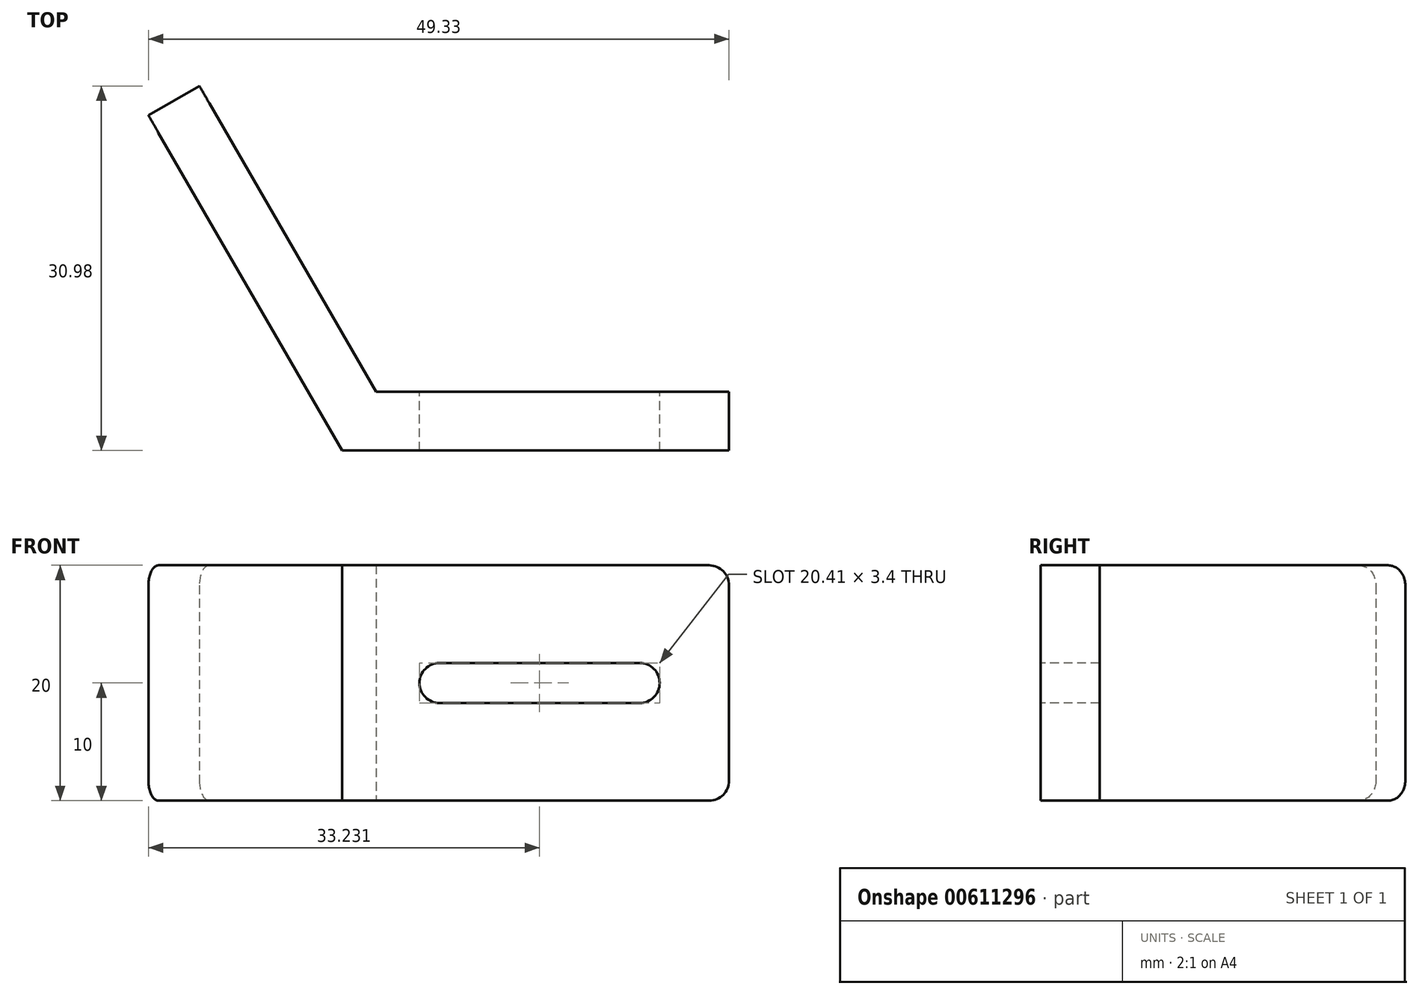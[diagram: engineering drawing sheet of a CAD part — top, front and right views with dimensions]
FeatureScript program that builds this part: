
annotation { "Feature Type Name" : "Feature", "Feature Type Description" : "" }
export const myFeature = defineFeature(function(context is Context, id is Id, definition is map)
    precondition{}
    {
        {
            var Q0;
            Q0=qCreatedBy(makeId("Top.planeOp"),FACE);
            var sketch = newSketch(context, id + "F0", { "sketchPlane" : qUnion([Q0])});
            skLineSegment(sketch, "E0", {"start": v(0, 0) * mm, "end": v(30, 0) * mm});
            skLineSegment(sketch, "E1", {"start": v(30, 0) * mm, "end": v(30, 5) * mm});
            skLineSegment(sketch, "E2", {"start": v(30, 5) * mm, "end": v(0, 5) * mm});
            skLineSegment(sketch, "E3", {"start": v(0, 5) * mm, "end": v(-15, 30.98) * mm});
            skLineSegment(sketch, "E4", {"start": v(-15, 30.98) * mm, "end": v(-19.33, 28.48) * mm});
            skLineSegment(sketch, "E5", {"start": v(0, 0) * mm, "end": v(-2.89, 0) * mm});
            skLineSegment(sketch, "E6", {"start": v(-2.89, 0) * mm, "end": v(-19.33, 28.48) * mm});
            skSolve(sketch);
        }
        {
            var Q0;
            Q0=makeQuery(id+"F0.imprint","IMPRINT",FACE,{"disambiguationData":[TD([[makeQuery(id+"F0.imprint","IMPRINT",EDGE,{"derivedFrom":sQuery(id+"F0.wireOp",EDGE,"E0")}),1.0]])]});
            extrude(context, id + "F1", {"entities" : qUnion([Q0]), "depth" : 20 * mm, "offsetDistance" : 25 * mm});
        }
        {
            var Q0;
            Q0=makeQuery(id+"F1.opExtrude","SWEPT_FACE",FACE,{"disambiguationData":[OSD([sQuery(id+"F0.wireOp",EDGE,"E0"),sQuery(id+"F0.wireOp",EDGE,"E5")])]});
            var sketch = newSketch(context, id + "F2", { "sketchPlane" : qUnion([Q0])});
            skLineSegment(sketch, "E7.bottom", {"start": v(24.1, 8.3) * mm, "end": v(3.7, 8.3) * mm});
            skLineSegment(sketch, "E7.top", {"start": v(24.1, 11.7) * mm, "end": v(3.7, 11.7) * mm});
            skLineSegment(sketch, "E7.left", {"start": v(24.1, 8.3) * mm, "end": v(24.1, 11.7) * mm});
            skLineSegment(sketch, "E7.right", {"start": v(3.7, 8.3) * mm, "end": v(3.7, 11.7) * mm});
            skPoint(sketch, "E7.middle", {"position": v(13.9, 10) * mm});
            skPoint(sketch, "E7.middle.positionSnap0", {"position": v(30, 10) * mm});
            skPoint(sketch, "E7.centerSnap0", {"position": v(30, 10) * mm});
            skSolve(sketch);
        }
        {
            var Q0;
            Q0=makeQuery(id+"F2.imprint","IMPRINT",FACE,{"disambiguationData":[TD([[makeQuery(id+"F2.imprint","IMPRINT",EDGE,{"derivedFrom":sQuery(id+"F2.wireOp",EDGE,"E7.bottom")}),-1.0]])]});
            extrude(context, id + "F3", {"entities" : qUnion([Q0]), "operationType" : NewBodyOperationType.REMOVE, "oppositeDirection" : true, "depth" : 25 * mm, "offsetDistance" : 25 * mm});
        }
        {
            var Q0;
            Q0=makeQuery(id+"F3.boolean.opBoolean","COPY",EDGE,{"derivedFrom":makeQuery(id+"F3.opExtrude","SWEPT_EDGE",EDGE,{"disambiguationData":[OSD([sQuery(id+"F2.wireOp",EDGE,"E7.bottom"),sQuery(id+"F2.wireOp",EDGE,"E7.right")])]})});
            var Q1;
            Q1=makeQuery(id+"F3.boolean.opBoolean","COPY",EDGE,{"derivedFrom":makeQuery(id+"F3.opExtrude","SWEPT_EDGE",EDGE,{"disambiguationData":[OSD([sQuery(id+"F2.wireOp",EDGE,"E7.top"),sQuery(id+"F2.wireOp",EDGE,"E7.right")])]})});
            var Q2;
            Q2=makeQuery(id+"F3.boolean.opBoolean","COPY",EDGE,{"derivedFrom":makeQuery(id+"F3.opExtrude","SWEPT_EDGE",EDGE,{"disambiguationData":[OSD([sQuery(id+"F2.wireOp",EDGE,"E7.top"),sQuery(id+"F2.wireOp",EDGE,"E7.left")])]})});
            var Q3;
            Q3=makeQuery(id+"F3.boolean.opBoolean","COPY",EDGE,{"derivedFrom":makeQuery(id+"F3.opExtrude","SWEPT_EDGE",EDGE,{"disambiguationData":[OSD([sQuery(id+"F2.wireOp",EDGE,"E7.bottom"),sQuery(id+"F2.wireOp",EDGE,"E7.left")])]})});
            var Q4;
            Q4=makeQuery(id+"F1.opExtrude","CAP_EDGE",EDGE,{"disambiguationData":[OSD([sQuery(id+"F0.wireOp",EDGE,"E1")])],"isStart":false});
            var Q5;
            Q5=makeQuery(id+"F1.opExtrude","CAP_EDGE",EDGE,{"disambiguationData":[OSD([sQuery(id+"F0.wireOp",EDGE,"E1")])],"isStart":true});
            var Q6;
            Q6=makeQuery(id+"F1.opExtrude","CAP_EDGE",EDGE,{"disambiguationData":[OSD([sQuery(id+"F0.wireOp",EDGE,"E4")])],"isStart":false});
            var Q7;
            Q7=makeQuery(id+"F1.opExtrude","CAP_EDGE",EDGE,{"disambiguationData":[OSD([sQuery(id+"F0.wireOp",EDGE,"E4")])],"isStart":true});
            fillet(context, id + "F4", {"entities" : qUnion([Q0, Q1, Q2, Q3, Q4, Q5, Q6, Q7]), "radius" : (3.4 / 2) * mm, "tangentPropagation" : true, "allowEdgeOverflow" : false});
        }
    });
